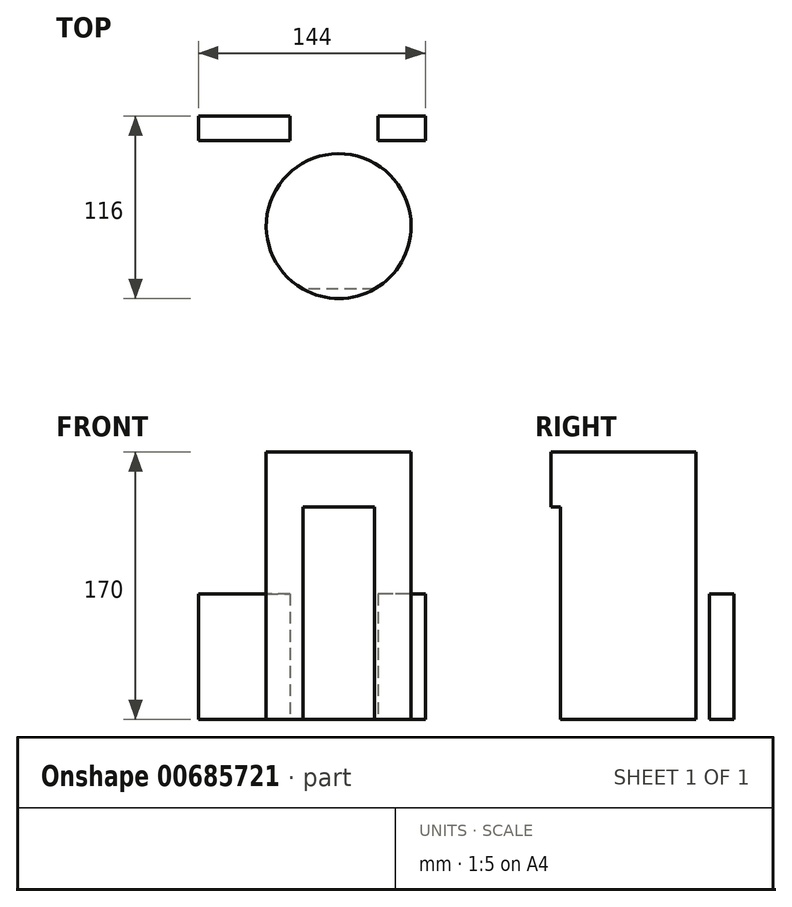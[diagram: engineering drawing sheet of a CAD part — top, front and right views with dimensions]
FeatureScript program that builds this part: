
annotation { "Feature Type Name" : "Feature", "Feature Type Description" : "" }
export const myFeature = defineFeature(function(context is Context, id is Id, definition is map)
    precondition{}
    {
        {
            var Q0;
            Q0=qCreatedBy(makeId("Top.planeOp"),FACE);
            var sketch = newSketch(context, id + "F0", { "sketchPlane" : qUnion([Q0])});
            skLineSegment(sketch, "E0.bottom", {"start": v(72, 55) * mm, "end": v(-72, 55) * mm});
            skLineSegment(sketch, "E0.top", {"start": v(72, -55) * mm, "end": v(-72, -55) * mm});
            skLineSegment(sketch, "E0.left", {"start": v(72, 55) * mm, "end": v(72, -55) * mm});
            skLineSegment(sketch, "E0.right", {"start": v(-72, 55) * mm, "end": v(-72, -55) * mm});
            skPoint(sketch, "E0.middle", {"position": v(0, 0) * mm});
            skLineSegment(sketch, "E1.bottom", {"start": v(-72, 55) * mm, "end": v(-13.9, 55) * mm});
            skLineSegment(sketch, "E1.top", {"start": v(-72, 39.43) * mm, "end": v(-13.9, 39.43) * mm});
            skLineSegment(sketch, "E1.left", {"start": v(-72, 55) * mm, "end": v(-72, 39.43) * mm});
            skLineSegment(sketch, "E1.right", {"start": v(-13.9, 55) * mm, "end": v(-13.9, 39.43) * mm});
            skLineSegment(sketch, "E2.bottom", {"start": v(72, 55) * mm, "end": v(41.93, 55) * mm});
            skLineSegment(sketch, "E2.top", {"start": v(72, 39.43) * mm, "end": v(41.93, 39.43) * mm});
            skLineSegment(sketch, "E2.left", {"start": v(72, 55) * mm, "end": v(72, 39.43) * mm});
            skLineSegment(sketch, "E2.right", {"start": v(41.93, 55) * mm, "end": v(41.93, 39.43) * mm});
            skCircle(sketch, "E3", {"center": v(17, -15) * mm, "radius": 46 * mm});
            skSolve(sketch);
        }
        {
            var Q0;
            Q0=makeQuery(id+"F0.imprint","IMPRINT",FACE,{"disambiguationData":[TD([[makeQuery(id+"F0.imprint","IMPRINT",EDGE,{"derivedFrom":sQuery(id+"F0.wireOp",EDGE,"E0.bottom")}),1.0]])]});
            extrude(context, id + "F1", {"entities" : qUnion([Q0]), "depth" : 80 * mm, "offsetDistance" : 25 * mm});
        }
        {
            var Q0;
            {var subQ0=sQuery(id+"F0.wireOp",EDGE,"E3");var subQ1=sQuery(id+"F0.wireOp",EDGE,"E0.top");var subQ2=makeQuery(id+"F0.imprint","INTERSECT",VERTEX,{"disambiguationData":[OD(0.0)],"derivedFrom":[subQ1,subQ0]});Q0=makeQuery(id+"F0.imprint","IMPRINT",FACE,{"disambiguationData":[TD([[makeQuery(id+"F0.imprint","IMPRINT",EDGE,{"disambiguationData":[TD([[subQ2,-1.0]])],"derivedFrom":subQ1}),1.0]])]});}
            var Q1;
            {var subQ0=sQuery(id+"F0.wireOp",EDGE,"E3");var subQ1=sQuery(id+"F0.wireOp",EDGE,"E0.top");var subQ2=makeQuery(id+"F0.imprint","INTERSECT",VERTEX,{"disambiguationData":[OD(0.0)],"derivedFrom":[subQ1,subQ0]});Q1=makeQuery(id+"F0.imprint","IMPRINT",FACE,{"disambiguationData":[TD([[makeQuery(id+"F0.imprint","IMPRINT",EDGE,{"disambiguationData":[TD([[subQ2,-1.0]])],"derivedFrom":subQ1}),-1.0]])]});}
            extrude(context, id + "F2", {"entities" : qUnion([Q0, Q1]), "operationType" : NewBodyOperationType.ADD, "depth" : 170 * mm, "offsetDistance" : 25 * mm});
        }
        {
            var Q0;
            {var subQ0=sQuery(id+"F0.wireOp",EDGE,"E3");var subQ1=sQuery(id+"F0.wireOp",EDGE,"E0.top");var subQ2=makeQuery(id+"F0.imprint","INTERSECT",VERTEX,{"disambiguationData":[OD(0.0)],"derivedFrom":[subQ1,subQ0]});Q0=makeQuery(id+"F0.imprint","IMPRINT",FACE,{"disambiguationData":[TD([[makeQuery(id+"F0.imprint","IMPRINT",EDGE,{"disambiguationData":[TD([[subQ2,-1.0]])],"derivedFrom":subQ1}),1.0]])]});}
            extrude(context, id + "F3", {"entities" : qUnion([Q0]), "operationType" : NewBodyOperationType.REMOVE, "depth" : 135 * mm, "offsetDistance" : 25 * mm});
        }
    });
